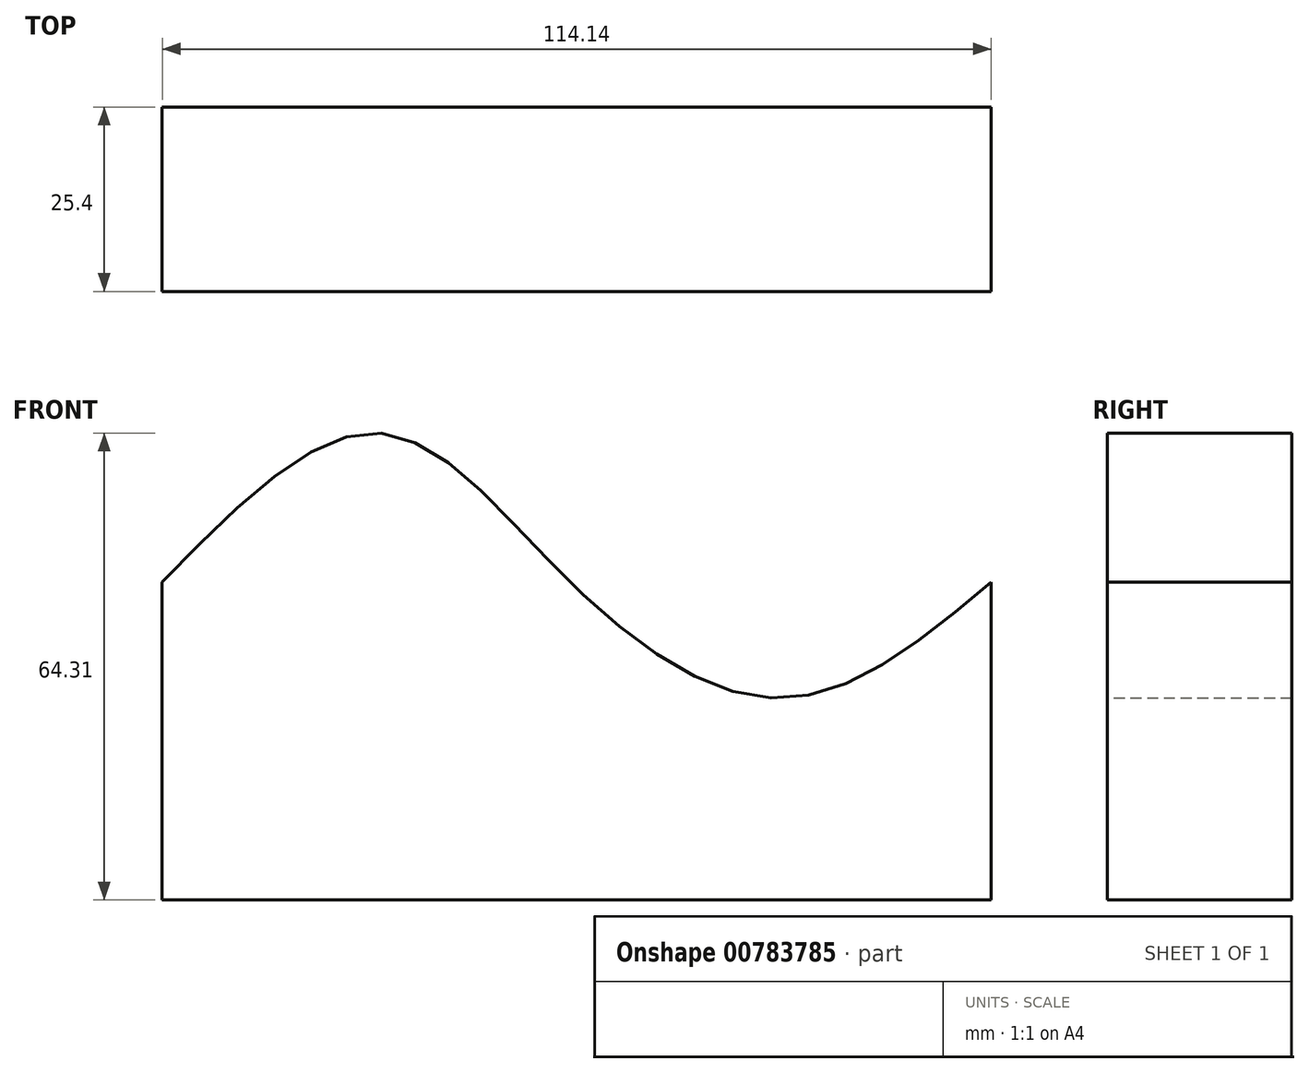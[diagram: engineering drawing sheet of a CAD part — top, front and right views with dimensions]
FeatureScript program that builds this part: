
annotation { "Feature Type Name" : "Feature", "Feature Type Description" : "" }
export const myFeature = defineFeature(function(context is Context, id is Id, definition is map)
    precondition{}
    {
        {
            var Q0;
            Q0=qCreatedBy(makeId("Front.planeOp"),FACE);
            var sketch = newSketch(context, id + "F0", { "sketchPlane" : qUnion([Q0])});
            skFitSpline(sketch, "E0", {"points": [v(-56.21, 0) * mm, v(-26.27, 20.53) * mm, v(0, 0) * mm, v(29.52, -15.96) * mm, v(57.93, 0) * mm], "startDerivative": vector(119.43, 122.7) * mm, "endDerivative": vector(114.14, 95.4) * mm});
            skLineSegment(sketch, "E1", {"start": v(-56.21, 0) * mm, "end": v(-56.21, -43.75) * mm});
            skLineSegment(sketch, "E2", {"start": v(57.93, 0) * mm, "end": v(57.93, -43.75) * mm});
            skLineSegment(sketch, "E3", {"start": v(57.93, -43.75) * mm, "end": v(-56.21, -43.75) * mm});
            skSolve(sketch);
        }
        {
            var Q0;
            Q0=makeQuery(id+"F0.imprint","IMPRINT",FACE,{"disambiguationData":[TD([[makeQuery(id+"F0.imprint","IMPRINT",EDGE,{"derivedFrom":sQuery(id+"F0.wireOp",EDGE,"E0")}),-1.0]])]});
            extrude(context, id + "F1", {"entities" : qUnion([Q0]), "depth" : 25.4 * mm, "offsetDistance" : 25.4 * mm});
        }
    });
